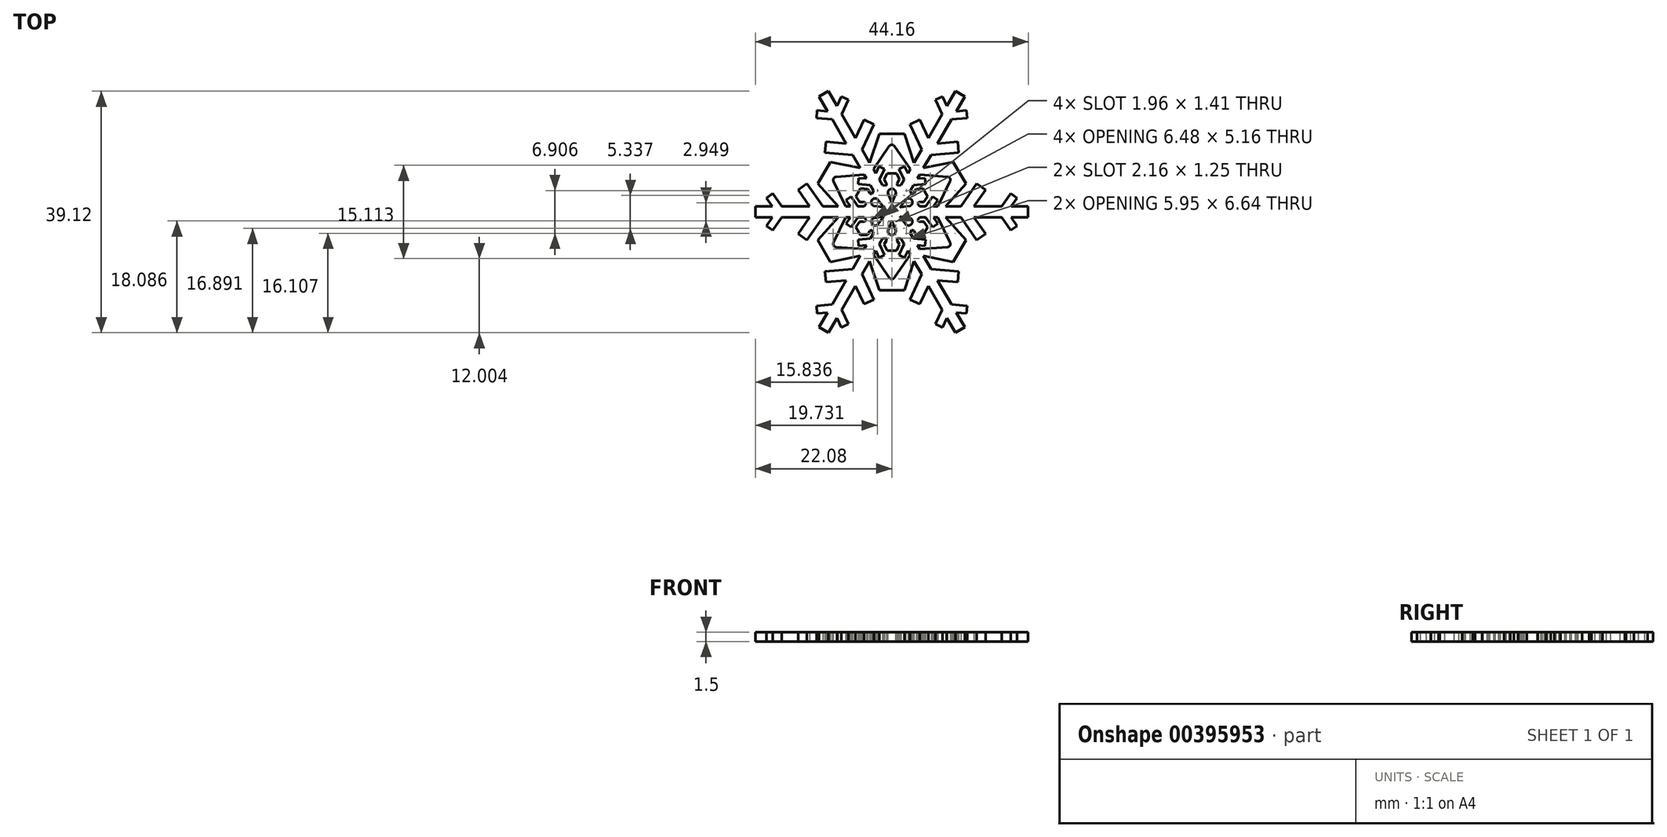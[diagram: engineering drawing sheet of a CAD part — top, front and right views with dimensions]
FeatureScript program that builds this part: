
annotation { "Feature Type Name" : "Feature", "Feature Type Description" : "" }
export const myFeature = defineFeature(function(context is Context, id is Id, definition is map)
    precondition{}
    {
        {
            var Q0;
            Q0=qCreatedBy(makeId("Top.planeOp"),FACE);
            var sketch = newSketch(context, id + "F0", { "sketchPlane" : qUnion([Q0])});
            skLineSegment(sketch, "E0.bottom", {"start": v(-43.7, 44.8) * mm, "end": v(41.1, 44.8) * mm});
            skLineSegment(sketch, "E0.top", {"start": v(-43.7, -40) * mm, "end": v(41.1, -40) * mm});
            skLineSegment(sketch, "E0.left", {"start": v(-43.7, 44.8) * mm, "end": v(-43.7, -40) * mm});
            skLineSegment(sketch, "E0.right", {"start": v(41.1, 44.8) * mm, "end": v(41.1, -40) * mm});
            skLineSegment(sketch, "E1", {"start": v(-44.15, 0) * mm, "end": v(-44.15, 1.75) * mm});
            skLineSegment(sketch, "E2", {"start": v(-44.15, 1.75) * mm, "end": v(-38.65, 1.75) * mm});
            skLineSegment(sketch, "E3", {"start": v(-38.65, 1.75) * mm, "end": v(-40.58, 4.5) * mm});
            skLineSegment(sketch, "E4", {"start": v(-40.58, 4.5) * mm, "end": v(-38.53, 5.94) * mm});
            skLineSegment(sketch, "E5", {"start": v(-38.53, 5.94) * mm, "end": v(-35.6, 1.75) * mm});
            skLineSegment(sketch, "E6", {"start": v(-35.6, 1.75) * mm, "end": v(-26.6, 1.75) * mm});
            skLineSegment(sketch, "E7", {"start": v(-26.6, 1.75) * mm, "end": v(-30.36, 7.13) * mm});
            skLineSegment(sketch, "E8", {"start": v(-30.36, 7.13) * mm, "end": v(-27.49, 9.13) * mm});
            skLineSegment(sketch, "E9", {"start": v(-27.49, 9.13) * mm, "end": v(-22.34, 1.75) * mm});
            skLineSegment(sketch, "E10", {"start": v(-22.34, 1.75) * mm, "end": v(-17.4, 1.75) * mm});
            skLineSegment(sketch, "E11", {"start": v(-14.94, 1.75) * mm, "end": v(-13.44, 1.75) * mm});
            skLineSegment(sketch, "E12", {"start": v(-13.44, 1.75) * mm, "end": v(-14.87, 3.8) * mm});
            skLineSegment(sketch, "E13", {"start": v(-14.87, 3.8) * mm, "end": v(-13.23, 4.94) * mm});
            skLineSegment(sketch, "E14", {"start": v(-13.23, 4.94) * mm, "end": v(-11, 1.75) * mm});
            skLineSegment(sketch, "E15", {"start": v(0, 0) * mm, "end": v(-44.15, 0) * mm, "construction": true});
            skLineSegment(sketch, "E16", {"start": v(-11, 1.75) * mm, "end": v(-8.98, 1.75) * mm});
            skLineSegment(sketch, "E17", {"start": v(0, 0) * mm, "end": v(-10.85, 6.27) * mm});
            skLineSegment(sketch, "E18", {"start": v(-8.98, 1.75) * mm, "end": v(-8.24, 2.67) * mm});
            skLineSegment(sketch, "E19", {"start": v(-8.24, 2.67) * mm, "end": v(-8.84, 3.15) * mm});
            skLineSegment(sketch, "E20", {"start": v(-8.84, 3.15) * mm, "end": v(-10.37, 3.15) * mm});
            skLineSegment(sketch, "E21", {"start": v(-10.37, 3.15) * mm, "end": v(-11.62, 4.94) * mm});
            skLineSegment(sketch, "E22", {"start": v(-11.62, 4.94) * mm, "end": v(-10.85, 6.27) * mm});
            skLineSegment(sketch, "E23", {"start": v(-10.85, 6.27) * mm, "end": v(-31.84, 18.38) * mm, "construction": true});
            skLineSegment(sketch, "E24", {"start": v(-23.98, 9.13) * mm, "end": v(-21.94, 12.67) * mm});
            skLineSegment(sketch, "E25", {"start": v(-14.94, 1.75) * mm, "end": v(-19.5, 11.26) * mm});
            skLineSegment(sketch, "E26", {"start": v(-23.98, 9.13) * mm, "end": v(-17.4, 1.75) * mm});
            skLineSegment(sketch, "E27", {"start": v(-21.94, 12.67) * mm, "end": v(-19.5, 11.26) * mm});
            skLineSegment(sketch, "E28.MirrorCS", {"start": v(0, 0) * mm, "end": v(-10.85, -6.27) * mm});
            skLineSegment(sketch, "E29.MirrorCS", {"start": v(-44.15, 0) * mm, "end": v(-44.15, -1.75) * mm});
            skLineSegment(sketch, "E30.MirrorCS", {"start": v(-14.94, -1.75) * mm, "end": v(-13.44, -1.75) * mm});
            skLineSegment(sketch, "E31.MirrorCS", {"start": v(-11.62, -4.94) * mm, "end": v(-10.85, -6.27) * mm});
            skLineSegment(sketch, "E32.MirrorCS", {"start": v(-14.87, -3.8) * mm, "end": v(-13.23, -4.94) * mm});
            skLineSegment(sketch, "E33.MirrorCS", {"start": v(-8.98, -1.75) * mm, "end": v(-8.24, -2.67) * mm});
            skLineSegment(sketch, "E34.MirrorCS", {"start": v(-8.84, -3.15) * mm, "end": v(-10.37, -3.15) * mm});
            skLineSegment(sketch, "E35.MirrorCS", {"start": v(-8.24, -2.67) * mm, "end": v(-8.84, -3.15) * mm});
            skLineSegment(sketch, "E36.MirrorCS", {"start": v(-14.94, -1.75) * mm, "end": v(-19.5, -11.26) * mm});
            skLineSegment(sketch, "E37.MirrorCS", {"start": v(-27.49, -9.13) * mm, "end": v(-22.34, -1.75) * mm});
            skLineSegment(sketch, "E38.MirrorCS", {"start": v(-21.94, -12.67) * mm, "end": v(-19.5, -11.26) * mm});
            skLineSegment(sketch, "E39.MirrorCS", {"start": v(-23.98, -9.13) * mm, "end": v(-21.94, -12.67) * mm});
            skLineSegment(sketch, "E40.MirrorCS", {"start": v(-11, -1.75) * mm, "end": v(-8.98, -1.75) * mm});
            skLineSegment(sketch, "E41.MirrorCS", {"start": v(-38.53, -5.94) * mm, "end": v(-35.6, -1.75) * mm});
            skLineSegment(sketch, "E42.MirrorCS", {"start": v(-40.58, -4.5) * mm, "end": v(-38.53, -5.94) * mm});
            skLineSegment(sketch, "E43.MirrorCS", {"start": v(-38.65, -1.75) * mm, "end": v(-40.58, -4.5) * mm});
            skLineSegment(sketch, "E44.MirrorCS", {"start": v(-44.15, -1.75) * mm, "end": v(-38.65, -1.75) * mm});
            skLineSegment(sketch, "E45.MirrorCS", {"start": v(-23.98, -9.13) * mm, "end": v(-17.4, -1.75) * mm});
            skLineSegment(sketch, "E46.MirrorCS", {"start": v(-30.36, -7.13) * mm, "end": v(-27.49, -9.13) * mm});
            skLineSegment(sketch, "E47.MirrorCS", {"start": v(-26.6, -1.75) * mm, "end": v(-30.36, -7.13) * mm});
            skLineSegment(sketch, "E48.MirrorCS", {"start": v(-35.6, -1.75) * mm, "end": v(-26.6, -1.75) * mm});
            skLineSegment(sketch, "E49.MirrorCS", {"start": v(-22.34, -1.75) * mm, "end": v(-17.4, -1.75) * mm});
            skLineSegment(sketch, "E50.MirrorCS", {"start": v(-13.44, -1.75) * mm, "end": v(-14.87, -3.8) * mm});
            skLineSegment(sketch, "E51.MirrorCS", {"start": v(-10.37, -3.15) * mm, "end": v(-11.62, -4.94) * mm});
            skLineSegment(sketch, "E52.MirrorCS", {"start": v(-13.23, -4.94) * mm, "end": v(-11, -1.75) * mm});
            skSolve(sketch);
        }
        {
            var Q0;
            Q0=makeQuery(id+"F0.imprint","IMPRINT",FACE,{"disambiguationData":[TD([[makeQuery(id+"F0.imprint","IMPRINT",EDGE,{"derivedFrom":sQuery(id+"F0.wireOp",EDGE,"E1")}),-1.0]])]});
            var Q1;
            {var subQ0=sQuery(id+"F0.wireOp",EDGE,"E3");Q1=makeQuery(id+"F0.imprint","IMPRINT",FACE,{"disambiguationData":[TD([[makeQuery(id+"F0.imprint","IMPRINT",EDGE,{"derivedFrom":subQ0}),-1.0]])]});}
            extrude(context, id + "F1", {"entities" : qUnion([Q0, Q1]), "endBound" : BoundingType.SYMMETRIC, "depth" : 3 * mm});
        }
        {
            var Q0;
            Q0=qCreatedBy(makeId("Right.planeOp"),FACE);
            var sketch = newSketch(context, id + "F2", { "sketchPlane" : qUnion([Q0])});
            skLineSegment(sketch, "E53", {"start": v(0, 0) * mm, "end": v(0, -43.45) * mm, "construction": true});
            skSolve(sketch);
        }
        {
            var Q0;
            Q0=makeQuery(id+"F1.opExtrude","SWEPT_BODY",BODY,{"disambiguationData":[OSD([sQuery(id+"F0.wireOp",EDGE,"E1"),sQuery(id+"F0.wireOp",EDGE,"E2"),sQuery(id+"F0.wireOp",EDGE,"E3"),sQuery(id+"F0.wireOp",EDGE,"E4"),sQuery(id+"F0.wireOp",EDGE,"E5"),sQuery(id+"F0.wireOp",EDGE,"E6"),sQuery(id+"F0.wireOp",EDGE,"E7"),sQuery(id+"F0.wireOp",EDGE,"E8"),sQuery(id+"F0.wireOp",EDGE,"E9"),sQuery(id+"F0.wireOp",EDGE,"E10"),sQuery(id+"F0.wireOp",EDGE,"189a7a4e-f39c-4bfd-b122-43a29ca94680"),sQuery(id+"F0.wireOp",EDGE,"67050dc1-3990-4a49-9707-dffdccfb30a0"),sQuery(id+"F0.wireOp",EDGE,"437a0215-fb6c-4063-ad75-b84b83856d58"),sQuery(id+"F0.wireOp",EDGE,"E11"),sQuery(id+"F0.wireOp",EDGE,"E12"),sQuery(id+"F0.wireOp",EDGE,"E13"),sQuery(id+"F0.wireOp",EDGE,"E14"),sQuery(id+"F0.wireOp",EDGE,"5e9898c1-a996-4e9f-834a-20b7154747a1"),sQuery(id+"F0.wireOp",EDGE,"4f175b08-8b9f-4015-be58-81c3dce13333"),sQuery(id+"F0.wireOp",EDGE,"3166d6ec-2b74-46b0-8a25-8ff819b97b050.MirrorCS"),sQuery(id+"F0.wireOp",EDGE,"3166d6ec-2b74-46b0-8a25-8ff819b97b051.MirrorCS"),sQuery(id+"F0.wireOp",EDGE,"3166d6ec-2b74-46b0-8a25-8ff819b97b052.MirrorCS"),sQuery(id+"F0.wireOp",EDGE,"3166d6ec-2b74-46b0-8a25-8ff819b97b053.MirrorCS"),sQuery(id+"F0.wireOp",EDGE,"3166d6ec-2b74-46b0-8a25-8ff819b97b054.MirrorCS"),sQuery(id+"F0.wireOp",EDGE,"3166d6ec-2b74-46b0-8a25-8ff819b97b055.MirrorCS"),sQuery(id+"F0.wireOp",EDGE,"3166d6ec-2b74-46b0-8a25-8ff819b97b056.MirrorCS"),sQuery(id+"F0.wireOp",EDGE,"3166d6ec-2b74-46b0-8a25-8ff819b97b057.MirrorCS"),sQuery(id+"F0.wireOp",EDGE,"3166d6ec-2b74-46b0-8a25-8ff819b97b058.MirrorCS"),sQuery(id+"F0.wireOp",EDGE,"3166d6ec-2b74-46b0-8a25-8ff819b97b059.MirrorCS"),sQuery(id+"F0.wireOp",EDGE,"3166d6ec-2b74-46b0-8a25-8ff819b97b0510.MirrorCS"),sQuery(id+"F0.wireOp",EDGE,"3166d6ec-2b74-46b0-8a25-8ff819b97b0511.MirrorCS"),sQuery(id+"F0.wireOp",EDGE,"3166d6ec-2b74-46b0-8a25-8ff819b97b0512.MirrorCS"),sQuery(id+"F0.wireOp",EDGE,"3166d6ec-2b74-46b0-8a25-8ff819b97b0513.MirrorCS"),sQuery(id+"F0.wireOp",EDGE,"3166d6ec-2b74-46b0-8a25-8ff819b97b0514.MirrorCS"),sQuery(id+"F0.wireOp",EDGE,"3166d6ec-2b74-46b0-8a25-8ff819b97b0515.MirrorCS"),sQuery(id+"F0.wireOp",EDGE,"3166d6ec-2b74-46b0-8a25-8ff819b97b0516.MirrorCS"),sQuery(id+"F0.wireOp",EDGE,"3166d6ec-2b74-46b0-8a25-8ff819b97b0517.MirrorCS"),sQuery(id+"F0.wireOp",EDGE,"3166d6ec-2b74-46b0-8a25-8ff819b97b0518.MirrorCS")])]});
            var Q1;
            Q1=sQuery(id+"F2.wireOp",EDGE,"E53");
            circularPattern(context, id + "F3", {"operationType" : NewBodyOperationType.ADD, "entities" : qUnion([Q0]), "axis" : qUnion([Q1]), "angle" : 60 * degree, "instanceCount" : 6});
        }
        {
            var Q0;
            {var subQ0=makeQuery(id+"F1.opExtrude","CAP_FACE",FACE,{"disambiguationData":[OSD([sQuery(id+"F0.wireOp",EDGE,"E1"),sQuery(id+"F0.wireOp",EDGE,"E2"),sQuery(id+"F0.wireOp",EDGE,"E3"),sQuery(id+"F0.wireOp",EDGE,"E4"),sQuery(id+"F0.wireOp",EDGE,"E5"),sQuery(id+"F0.wireOp",EDGE,"E6"),sQuery(id+"F0.wireOp",EDGE,"E7"),sQuery(id+"F0.wireOp",EDGE,"E8"),sQuery(id+"F0.wireOp",EDGE,"E9"),sQuery(id+"F0.wireOp",EDGE,"E10"),sQuery(id+"F0.wireOp",EDGE,"189a7a4e-f39c-4bfd-b122-43a29ca94680"),sQuery(id+"F0.wireOp",EDGE,"67050dc1-3990-4a49-9707-dffdccfb30a0"),sQuery(id+"F0.wireOp",EDGE,"437a0215-fb6c-4063-ad75-b84b83856d58"),sQuery(id+"F0.wireOp",EDGE,"E11"),sQuery(id+"F0.wireOp",EDGE,"E12"),sQuery(id+"F0.wireOp",EDGE,"E13"),sQuery(id+"F0.wireOp",EDGE,"E14"),sQuery(id+"F0.wireOp",EDGE,"E16"),sQuery(id+"F0.wireOp",EDGE,"E17"),sQuery(id+"F0.wireOp",EDGE,"E18"),sQuery(id+"F0.wireOp",EDGE,"E19"),sQuery(id+"F0.wireOp",EDGE,"E20"),sQuery(id+"F0.wireOp",EDGE,"E21"),sQuery(id+"F0.wireOp",EDGE,"E22"),sQuery(id+"F0.wireOp",EDGE,"0c32c283-354d-45ec-8926-575daeb4bd260.MirrorCS"),sQuery(id+"F0.wireOp",EDGE,"0c32c283-354d-45ec-8926-575daeb4bd261.MirrorCS"),sQuery(id+"F0.wireOp",EDGE,"0c32c283-354d-45ec-8926-575daeb4bd262.MirrorCS"),sQuery(id+"F0.wireOp",EDGE,"0c32c283-354d-45ec-8926-575daeb4bd263.MirrorCS"),sQuery(id+"F0.wireOp",EDGE,"0c32c283-354d-45ec-8926-575daeb4bd264.MirrorCS"),sQuery(id+"F0.wireOp",EDGE,"0c32c283-354d-45ec-8926-575daeb4bd265.MirrorCS"),sQuery(id+"F0.wireOp",EDGE,"0c32c283-354d-45ec-8926-575daeb4bd266.MirrorCS"),sQuery(id+"F0.wireOp",EDGE,"0c32c283-354d-45ec-8926-575daeb4bd267.MirrorCS"),sQuery(id+"F0.wireOp",EDGE,"0c32c283-354d-45ec-8926-575daeb4bd268.MirrorCS"),sQuery(id+"F0.wireOp",EDGE,"0c32c283-354d-45ec-8926-575daeb4bd269.MirrorCS"),sQuery(id+"F0.wireOp",EDGE,"0c32c283-354d-45ec-8926-575daeb4bd2610.MirrorCS"),sQuery(id+"F0.wireOp",EDGE,"0c32c283-354d-45ec-8926-575daeb4bd2611.MirrorCS"),sQuery(id+"F0.wireOp",EDGE,"0c32c283-354d-45ec-8926-575daeb4bd2612.MirrorCS"),sQuery(id+"F0.wireOp",EDGE,"0c32c283-354d-45ec-8926-575daeb4bd2613.MirrorCS"),sQuery(id+"F0.wireOp",EDGE,"0c32c283-354d-45ec-8926-575daeb4bd2614.MirrorCS"),sQuery(id+"F0.wireOp",EDGE,"0c32c283-354d-45ec-8926-575daeb4bd2615.MirrorCS"),sQuery(id+"F0.wireOp",EDGE,"0c32c283-354d-45ec-8926-575daeb4bd2616.MirrorCS"),sQuery(id+"F0.wireOp",EDGE,"0c32c283-354d-45ec-8926-575daeb4bd2617.MirrorCS"),sQuery(id+"F0.wireOp",EDGE,"0c32c283-354d-45ec-8926-575daeb4bd2618.MirrorCS"),sQuery(id+"F0.wireOp",EDGE,"0c32c283-354d-45ec-8926-575daeb4bd2619.MirrorCS"),sQuery(id+"F0.wireOp",EDGE,"0c32c283-354d-45ec-8926-575daeb4bd2620.MirrorCS"),sQuery(id+"F0.wireOp",EDGE,"0c32c283-354d-45ec-8926-575daeb4bd2621.MirrorCS"),sQuery(id+"F0.wireOp",EDGE,"0c32c283-354d-45ec-8926-575daeb4bd2622.MirrorCS"),sQuery(id+"F0.wireOp",EDGE,"0c32c283-354d-45ec-8926-575daeb4bd2623.MirrorCS")])],"isStart":false});Q0=makeQuery(id+"F3.boolean.opBoolean","MERGE",FACE,{"derivedFrom":[subQ0,makeQuery(id+"F3.opPattern","COPY",FACE,{"derivedFrom":subQ0,"instanceName":"1"}),makeQuery(id+"F3.opPattern","COPY",FACE,{"derivedFrom":subQ0,"instanceName":"2"}),makeQuery(id+"F3.opPattern","COPY",FACE,{"derivedFrom":subQ0,"instanceName":"3"}),makeQuery(id+"F3.opPattern","COPY",FACE,{"derivedFrom":subQ0,"instanceName":"4"}),makeQuery(id+"F3.opPattern","COPY",FACE,{"derivedFrom":subQ0,"instanceName":"5"})]});}
            var sketch = newSketch(context, id + "F4", { "sketchPlane" : qUnion([Q0])});
            skLineSegment(sketch, "E54", {"start": v(0, 0) * mm, "end": v(-10.85, 6.27) * mm, "construction": true});
            skLineSegment(sketch, "E55", {"start": v(-6.5, 3.75) * mm, "end": v(-2.6, 1.5) * mm, "construction": true});
            skLineSegment(sketch, "E56", {"start": v(-5.87, 1.94) * mm, "end": v(-2.6, 1.5) * mm});
            skLineSegment(sketch, "E57.MirrorCS", {"start": v(-4.62, 4.1) * mm, "end": v(-2.6, 1.5) * mm});
            skLineSegment(sketch, "E58", {"start": v(-5.87, 1.94) * mm, "end": v(-4.62, 4.1) * mm, "construction": true});
            skArc(sketch, "E59", {"start": v(-4.62, 4.1) * mm, "mid": v(-6.5, 3.75) * mm, "end": v(-5.87, 1.94) * mm});
            skSolve(sketch);
        }
        {
            var Q0;
            Q0=makeQuery(id+"F4.imprint","IMPRINT",FACE,{"disambiguationData":[TD([[makeQuery(id+"F4.imprint","IMPRINT",EDGE,{"derivedFrom":sQuery(id+"F4.wireOp",EDGE,"980073ca-cf30-472a-b92e-9ee7ff5da41c")}),1.0]])]});
            var Q1;
            Q1=makeQuery(id+"F4.imprint","IMPRINT",FACE,{"disambiguationData":[TD([[makeQuery(id+"F4.imprint","IMPRINT",EDGE,{"derivedFrom":sQuery(id+"F4.wireOp",EDGE,"E56")}),1.0]])]});
            extrude(context, id + "F5", {"entities" : qUnion([Q0, Q1]), "operationType" : NewBodyOperationType.REMOVE, "endBound" : BoundingType.UP_TO_NEXT, "oppositeDirection" : true, "depth" : 25 * mm});
        }
        {
            var Q0;
            Q0=makeQuery(id+"F5.boolean.opBoolean","COPY",EDGE,{"derivedFrom":makeQuery(id+"F5.opExtrude","SWEPT_EDGE",EDGE,{"disambiguationData":[OSD([sQuery(id+"F4.wireOp",EDGE,"E56"),sQuery(id+"F4.wireOp",EDGE,"E57.MirrorCS")])]})});
            fillet(context, id + "F6", {"entities" : qUnion([Q0]), "radius" : 0.1 * mm, "tangentPropagation" : true, "allowEdgeOverflow" : false});
        }
        {
            var Q0;
            Q0=makeQuery(id+"F5.boolean.opBoolean","COPY",FACE,{"derivedFrom":makeQuery(id+"F5.opExtrude","SWEPT_FACE",FACE,{"disambiguationData":[OSD([sQuery(id+"F4.wireOp",EDGE,"E59")])]})});
            var Q1;
            Q1=makeQuery(id+"F5.boolean.opBoolean","COPY",FACE,{"derivedFrom":makeQuery(id+"F5.opExtrude","SWEPT_FACE",FACE,{"disambiguationData":[OSD([sQuery(id+"F4.wireOp",EDGE,"E56")])]})});
            var Q2;
            Q2=makeQuery(id+"F5.boolean.opBoolean","COPY",FACE,{"derivedFrom":makeQuery(id+"F5.opExtrude","SWEPT_FACE",FACE,{"disambiguationData":[OSD([sQuery(id+"F4.wireOp",EDGE,"E57.MirrorCS")])]})});
            var Q3;
            Q3=makeQuery(id+"F6.opFillet","BLEND_FACE",FACE,{"disambiguationData":[OSD([sQuery(id+"F4.wireOp",EDGE,"E56"),sQuery(id+"F4.wireOp",EDGE,"E57.MirrorCS")])]});
            var Q4;
            Q4=sQuery(id+"F2.wireOp",EDGE,"E53");
            circularPattern(context, id + "F7", {"faces" : qUnion([Q0, Q1, Q2, Q3]), "axis" : qUnion([Q4]), "angle" : 60 * degree, "instanceCount" : 6, "patternType" : PatternType.FACE});
        }
        {
            var Q0;
            {var subQ0=makeQuery(id+"F1.opExtrude","CAP_FACE",FACE,{"disambiguationData":[OSD([sQuery(id+"F0.wireOp",EDGE,"E1"),sQuery(id+"F0.wireOp",EDGE,"E2"),sQuery(id+"F0.wireOp",EDGE,"E3"),sQuery(id+"F0.wireOp",EDGE,"E4"),sQuery(id+"F0.wireOp",EDGE,"E5"),sQuery(id+"F0.wireOp",EDGE,"E6"),sQuery(id+"F0.wireOp",EDGE,"E7"),sQuery(id+"F0.wireOp",EDGE,"E8"),sQuery(id+"F0.wireOp",EDGE,"E9"),sQuery(id+"F0.wireOp",EDGE,"E10"),sQuery(id+"F0.wireOp",EDGE,"189a7a4e-f39c-4bfd-b122-43a29ca94680"),sQuery(id+"F0.wireOp",EDGE,"67050dc1-3990-4a49-9707-dffdccfb30a0"),sQuery(id+"F0.wireOp",EDGE,"437a0215-fb6c-4063-ad75-b84b83856d58"),sQuery(id+"F0.wireOp",EDGE,"E11"),sQuery(id+"F0.wireOp",EDGE,"E12"),sQuery(id+"F0.wireOp",EDGE,"E13"),sQuery(id+"F0.wireOp",EDGE,"E14"),sQuery(id+"F0.wireOp",EDGE,"E16"),sQuery(id+"F0.wireOp",EDGE,"E17"),sQuery(id+"F0.wireOp",EDGE,"E18"),sQuery(id+"F0.wireOp",EDGE,"E19"),sQuery(id+"F0.wireOp",EDGE,"E20"),sQuery(id+"F0.wireOp",EDGE,"E21"),sQuery(id+"F0.wireOp",EDGE,"E22"),sQuery(id+"F0.wireOp",EDGE,"0c32c283-354d-45ec-8926-575daeb4bd260.MirrorCS"),sQuery(id+"F0.wireOp",EDGE,"0c32c283-354d-45ec-8926-575daeb4bd261.MirrorCS"),sQuery(id+"F0.wireOp",EDGE,"0c32c283-354d-45ec-8926-575daeb4bd262.MirrorCS"),sQuery(id+"F0.wireOp",EDGE,"0c32c283-354d-45ec-8926-575daeb4bd263.MirrorCS"),sQuery(id+"F0.wireOp",EDGE,"0c32c283-354d-45ec-8926-575daeb4bd264.MirrorCS"),sQuery(id+"F0.wireOp",EDGE,"0c32c283-354d-45ec-8926-575daeb4bd265.MirrorCS"),sQuery(id+"F0.wireOp",EDGE,"0c32c283-354d-45ec-8926-575daeb4bd266.MirrorCS"),sQuery(id+"F0.wireOp",EDGE,"0c32c283-354d-45ec-8926-575daeb4bd267.MirrorCS"),sQuery(id+"F0.wireOp",EDGE,"0c32c283-354d-45ec-8926-575daeb4bd268.MirrorCS"),sQuery(id+"F0.wireOp",EDGE,"0c32c283-354d-45ec-8926-575daeb4bd269.MirrorCS"),sQuery(id+"F0.wireOp",EDGE,"0c32c283-354d-45ec-8926-575daeb4bd2610.MirrorCS"),sQuery(id+"F0.wireOp",EDGE,"0c32c283-354d-45ec-8926-575daeb4bd2611.MirrorCS"),sQuery(id+"F0.wireOp",EDGE,"0c32c283-354d-45ec-8926-575daeb4bd2612.MirrorCS"),sQuery(id+"F0.wireOp",EDGE,"0c32c283-354d-45ec-8926-575daeb4bd2613.MirrorCS"),sQuery(id+"F0.wireOp",EDGE,"0c32c283-354d-45ec-8926-575daeb4bd2614.MirrorCS"),sQuery(id+"F0.wireOp",EDGE,"0c32c283-354d-45ec-8926-575daeb4bd2615.MirrorCS"),sQuery(id+"F0.wireOp",EDGE,"0c32c283-354d-45ec-8926-575daeb4bd2616.MirrorCS"),sQuery(id+"F0.wireOp",EDGE,"0c32c283-354d-45ec-8926-575daeb4bd2617.MirrorCS"),sQuery(id+"F0.wireOp",EDGE,"0c32c283-354d-45ec-8926-575daeb4bd2618.MirrorCS"),sQuery(id+"F0.wireOp",EDGE,"0c32c283-354d-45ec-8926-575daeb4bd2619.MirrorCS"),sQuery(id+"F0.wireOp",EDGE,"0c32c283-354d-45ec-8926-575daeb4bd2620.MirrorCS"),sQuery(id+"F0.wireOp",EDGE,"0c32c283-354d-45ec-8926-575daeb4bd2621.MirrorCS"),sQuery(id+"F0.wireOp",EDGE,"0c32c283-354d-45ec-8926-575daeb4bd2622.MirrorCS"),sQuery(id+"F0.wireOp",EDGE,"0c32c283-354d-45ec-8926-575daeb4bd2623.MirrorCS")])],"isStart":false});Q0=makeQuery(id+"F3.boolean.opBoolean","MERGE",FACE,{"derivedFrom":[subQ0,makeQuery(id+"F3.opPattern","COPY",FACE,{"derivedFrom":subQ0,"instanceName":"1"}),makeQuery(id+"F3.opPattern","COPY",FACE,{"derivedFrom":subQ0,"instanceName":"2"}),makeQuery(id+"F3.opPattern","COPY",FACE,{"derivedFrom":subQ0,"instanceName":"3"}),makeQuery(id+"F3.opPattern","COPY",FACE,{"derivedFrom":subQ0,"instanceName":"4"}),makeQuery(id+"F3.opPattern","COPY",FACE,{"derivedFrom":subQ0,"instanceName":"5"})]});}
            var sketch = newSketch(context, id + "F8", { "sketchPlane" : qUnion([Q0])});
            skArc(sketch, "E60", {"start": v(-44.15, 1.75) * mm, "mid": v(-51.75, 0) * mm, "end": v(-44.15, -1.75) * mm});
            skCircle(sketch, "E61", {"center": v(-47.75, 0) * mm, "radius": 2 * mm});
            skSolve(sketch);
        }
        {
            var Q0;
            Q0=makeQuery(id+"F8.imprint","IMPRINT",FACE,{"disambiguationData":[TD([[makeQuery(id+"F8.imprint","IMPRINT",EDGE,{"derivedFrom":sQuery(id+"F8.wireOp",EDGE,"E60")}),1.0]])]});
            extrude(context, id + "F9", {"entities" : qUnion([Q0]), "operationType" : NewBodyOperationType.ADD, "oppositeDirection" : true, "depth" : 3 * mm});
        }
        {
            var Q0;
            Q0=makeQuery(id+"F3.boolean.opBoolean","MERGE",EDGE,{"derivedFrom":[makeQuery(id+"F1.opExtrude","SWEPT_EDGE",EDGE,{"disambiguationData":[OSD([sQuery(id+"F0.wireOp",EDGE,"E25"),sQuery(id+"F0.wireOp",EDGE,"E27")])]}),makeQuery(id+"F3.opPattern","COPY",EDGE,{"derivedFrom":makeQuery(id+"F1.opExtrude","SWEPT_EDGE",EDGE,{"disambiguationData":[OSD([sQuery(id+"F0.wireOp",EDGE,"E36.MirrorCS"),sQuery(id+"F0.wireOp",EDGE,"E38.MirrorCS")])]}),"instanceName":"1"})]});
            var Q1;
            Q1=makeQuery(id+"F3.boolean.opBoolean","MERGE",EDGE,{"derivedFrom":[makeQuery(id+"F1.opExtrude","SWEPT_EDGE",EDGE,{"disambiguationData":[OSD([sQuery(id+"F0.wireOp",EDGE,"E36.MirrorCS"),sQuery(id+"F0.wireOp",EDGE,"E38.MirrorCS")])]}),makeQuery(id+"F3.opPattern","COPY",EDGE,{"derivedFrom":makeQuery(id+"F1.opExtrude","SWEPT_EDGE",EDGE,{"disambiguationData":[OSD([sQuery(id+"F0.wireOp",EDGE,"E25"),sQuery(id+"F0.wireOp",EDGE,"E27")])]}),"instanceName":"5"})]});
            var Q2;
            Q2=makeQuery(id+"F3.boolean.opBoolean","MERGE",EDGE,{"derivedFrom":[makeQuery(id+"F3.opPattern","COPY",EDGE,{"derivedFrom":makeQuery(id+"F1.opExtrude","SWEPT_EDGE",EDGE,{"disambiguationData":[OSD([sQuery(id+"F0.wireOp",EDGE,"E25"),sQuery(id+"F0.wireOp",EDGE,"E27")])]}),"instanceName":"4"}),makeQuery(id+"F3.opPattern","COPY",EDGE,{"derivedFrom":makeQuery(id+"F1.opExtrude","SWEPT_EDGE",EDGE,{"disambiguationData":[OSD([sQuery(id+"F0.wireOp",EDGE,"E36.MirrorCS"),sQuery(id+"F0.wireOp",EDGE,"E38.MirrorCS")])]}),"instanceName":"5"})]});
            var Q3;
            Q3=makeQuery(id+"F3.boolean.opBoolean","MERGE",EDGE,{"derivedFrom":[makeQuery(id+"F3.opPattern","COPY",EDGE,{"derivedFrom":makeQuery(id+"F1.opExtrude","SWEPT_EDGE",EDGE,{"disambiguationData":[OSD([sQuery(id+"F0.wireOp",EDGE,"E25"),sQuery(id+"F0.wireOp",EDGE,"E27")])]}),"instanceName":"3"}),makeQuery(id+"F3.opPattern","COPY",EDGE,{"derivedFrom":makeQuery(id+"F1.opExtrude","SWEPT_EDGE",EDGE,{"disambiguationData":[OSD([sQuery(id+"F0.wireOp",EDGE,"E36.MirrorCS"),sQuery(id+"F0.wireOp",EDGE,"E38.MirrorCS")])]}),"instanceName":"4"})]});
            var Q4;
            Q4=makeQuery(id+"F3.boolean.opBoolean","MERGE",EDGE,{"derivedFrom":[makeQuery(id+"F3.opPattern","COPY",EDGE,{"derivedFrom":makeQuery(id+"F1.opExtrude","SWEPT_EDGE",EDGE,{"disambiguationData":[OSD([sQuery(id+"F0.wireOp",EDGE,"E25"),sQuery(id+"F0.wireOp",EDGE,"E27")])]}),"instanceName":"1"}),makeQuery(id+"F3.opPattern","COPY",EDGE,{"derivedFrom":makeQuery(id+"F1.opExtrude","SWEPT_EDGE",EDGE,{"disambiguationData":[OSD([sQuery(id+"F0.wireOp",EDGE,"E36.MirrorCS"),sQuery(id+"F0.wireOp",EDGE,"E38.MirrorCS")])]}),"instanceName":"2"})]});
            var Q5;
            Q5=makeQuery(id+"F3.boolean.opBoolean","MERGE",EDGE,{"derivedFrom":[makeQuery(id+"F3.opPattern","COPY",EDGE,{"derivedFrom":makeQuery(id+"F1.opExtrude","SWEPT_EDGE",EDGE,{"disambiguationData":[OSD([sQuery(id+"F0.wireOp",EDGE,"E25"),sQuery(id+"F0.wireOp",EDGE,"E27")])]}),"instanceName":"2"}),makeQuery(id+"F3.opPattern","COPY",EDGE,{"derivedFrom":makeQuery(id+"F1.opExtrude","SWEPT_EDGE",EDGE,{"disambiguationData":[OSD([sQuery(id+"F0.wireOp",EDGE,"E36.MirrorCS"),sQuery(id+"F0.wireOp",EDGE,"E38.MirrorCS")])]}),"instanceName":"3"})]});
            fillet(context, id + "F10", {"entities" : qUnion([Q0, Q1, Q2, Q3, Q4, Q5]), "radius" : 1 * mm, "tangentPropagation" : true, "allowEdgeOverflow" : false});
        }
        {
            var Q0;
            {var subQ0=sQuery(id+"F0.wireOp",EDGE,"E29.MirrorCS");var subQ1=sQuery(id+"F0.wireOp",EDGE,"E1");var subQ2=makeQuery(id+"F1.opExtrude","CAP_FACE",FACE,{"disambiguationData":[OSD([subQ1,sQuery(id+"F0.wireOp",EDGE,"E2"),sQuery(id+"F0.wireOp",EDGE,"E3"),sQuery(id+"F0.wireOp",EDGE,"E4"),sQuery(id+"F0.wireOp",EDGE,"E5"),sQuery(id+"F0.wireOp",EDGE,"E6"),sQuery(id+"F0.wireOp",EDGE,"E7"),sQuery(id+"F0.wireOp",EDGE,"E8"),sQuery(id+"F0.wireOp",EDGE,"E9"),sQuery(id+"F0.wireOp",EDGE,"E10"),sQuery(id+"F0.wireOp",EDGE,"E11"),sQuery(id+"F0.wireOp",EDGE,"E12"),sQuery(id+"F0.wireOp",EDGE,"E13"),sQuery(id+"F0.wireOp",EDGE,"E14"),sQuery(id+"F0.wireOp",EDGE,"E16"),sQuery(id+"F0.wireOp",EDGE,"E17"),sQuery(id+"F0.wireOp",EDGE,"E18"),sQuery(id+"F0.wireOp",EDGE,"E19"),sQuery(id+"F0.wireOp",EDGE,"E20"),sQuery(id+"F0.wireOp",EDGE,"E21"),sQuery(id+"F0.wireOp",EDGE,"E22"),sQuery(id+"F0.wireOp",EDGE,"E24"),sQuery(id+"F0.wireOp",EDGE,"E25"),sQuery(id+"F0.wireOp",EDGE,"E26"),sQuery(id+"F0.wireOp",EDGE,"E27"),sQuery(id+"F0.wireOp",EDGE,"E28.MirrorCS"),subQ0,sQuery(id+"F0.wireOp",EDGE,"E30.MirrorCS"),sQuery(id+"F0.wireOp",EDGE,"E31.MirrorCS"),sQuery(id+"F0.wireOp",EDGE,"E32.MirrorCS"),sQuery(id+"F0.wireOp",EDGE,"E33.MirrorCS"),sQuery(id+"F0.wireOp",EDGE,"E34.MirrorCS"),sQuery(id+"F0.wireOp",EDGE,"E35.MirrorCS"),sQuery(id+"F0.wireOp",EDGE,"E36.MirrorCS"),sQuery(id+"F0.wireOp",EDGE,"E37.MirrorCS"),sQuery(id+"F0.wireOp",EDGE,"E38.MirrorCS"),sQuery(id+"F0.wireOp",EDGE,"E39.MirrorCS"),sQuery(id+"F0.wireOp",EDGE,"E40.MirrorCS"),sQuery(id+"F0.wireOp",EDGE,"E41.MirrorCS"),sQuery(id+"F0.wireOp",EDGE,"E42.MirrorCS"),sQuery(id+"F0.wireOp",EDGE,"E43.MirrorCS"),sQuery(id+"F0.wireOp",EDGE,"E44.MirrorCS"),sQuery(id+"F0.wireOp",EDGE,"E45.MirrorCS"),sQuery(id+"F0.wireOp",EDGE,"E46.MirrorCS"),sQuery(id+"F0.wireOp",EDGE,"E47.MirrorCS"),sQuery(id+"F0.wireOp",EDGE,"E48.MirrorCS"),sQuery(id+"F0.wireOp",EDGE,"E49.MirrorCS"),sQuery(id+"F0.wireOp",EDGE,"E50.MirrorCS"),sQuery(id+"F0.wireOp",EDGE,"E51.MirrorCS"),sQuery(id+"F0.wireOp",EDGE,"E52.MirrorCS")])],"isStart":false});Q0=makeQuery(id+"F9.boolean.opBoolean","MERGE",FACE,{"derivedFrom":[makeQuery(id+"F3.boolean.opBoolean","MERGE",FACE,{"derivedFrom":[subQ2,makeQuery(id+"F3.opPattern","COPY",FACE,{"derivedFrom":subQ2,"instanceName":"1"}),makeQuery(id+"F3.opPattern","COPY",FACE,{"derivedFrom":subQ2,"instanceName":"2"}),makeQuery(id+"F3.opPattern","COPY",FACE,{"derivedFrom":subQ2,"instanceName":"3"}),makeQuery(id+"F3.opPattern","COPY",FACE,{"derivedFrom":subQ2,"instanceName":"4"}),makeQuery(id+"F3.opPattern","COPY",FACE,{"derivedFrom":subQ2,"instanceName":"5"})]}),makeQuery(id+"F9.opExtrude","CAP_FACE",FACE,{"disambiguationData":[OSD([subQ1,subQ0,sQuery(id+"F8.wireOp",EDGE,"E60"),sQuery(id+"F8.wireOp",EDGE,"E61")])],"isStart":true})]});}
            var sketch = newSketch(context, id + "F11", { "sketchPlane" : qUnion([Q0])});
            skLineSegment(sketch, "E62", {"start": v(-44.15, -1.75) * mm, "end": v(-44.15, 1.75) * mm});
            skSolve(sketch);
        }
        {
            var Q0;
            Q0=makeQuery(id+"F11.imprint","IMPRINT",FACE,{"disambiguationData":[TD([[makeQuery(id+"F11.imprint","IMPRINT",EDGE,{"derivedFrom":sQuery(id+"F11.wireOp",EDGE,"E62")}),1.0]])]});
            extrude(context, id + "F12", {"entities" : qUnion([Q0]), "operationType" : NewBodyOperationType.REMOVE, "oppositeDirection" : true, "depth" : 25 * mm});
        }
        {
            var Q0;
            Q0=makeQuery(id+"F1.opExtrude","SWEPT_BODY",BODY,{"disambiguationData":[OSD([sQuery(id+"F0.wireOp",EDGE,"E1"),sQuery(id+"F0.wireOp",EDGE,"E2"),sQuery(id+"F0.wireOp",EDGE,"E3"),sQuery(id+"F0.wireOp",EDGE,"E4"),sQuery(id+"F0.wireOp",EDGE,"E5"),sQuery(id+"F0.wireOp",EDGE,"E6"),sQuery(id+"F0.wireOp",EDGE,"E7"),sQuery(id+"F0.wireOp",EDGE,"E8"),sQuery(id+"F0.wireOp",EDGE,"E9"),sQuery(id+"F0.wireOp",EDGE,"E10"),sQuery(id+"F0.wireOp",EDGE,"E11"),sQuery(id+"F0.wireOp",EDGE,"E12"),sQuery(id+"F0.wireOp",EDGE,"E13"),sQuery(id+"F0.wireOp",EDGE,"E14"),sQuery(id+"F0.wireOp",EDGE,"E16"),sQuery(id+"F0.wireOp",EDGE,"E17"),sQuery(id+"F0.wireOp",EDGE,"E18"),sQuery(id+"F0.wireOp",EDGE,"E19"),sQuery(id+"F0.wireOp",EDGE,"E20"),sQuery(id+"F0.wireOp",EDGE,"E21"),sQuery(id+"F0.wireOp",EDGE,"E22"),sQuery(id+"F0.wireOp",EDGE,"E24"),sQuery(id+"F0.wireOp",EDGE,"E25"),sQuery(id+"F0.wireOp",EDGE,"E26"),sQuery(id+"F0.wireOp",EDGE,"E27"),sQuery(id+"F0.wireOp",EDGE,"E28.MirrorCS"),sQuery(id+"F0.wireOp",EDGE,"E29.MirrorCS"),sQuery(id+"F0.wireOp",EDGE,"E30.MirrorCS"),sQuery(id+"F0.wireOp",EDGE,"E31.MirrorCS"),sQuery(id+"F0.wireOp",EDGE,"E32.MirrorCS"),sQuery(id+"F0.wireOp",EDGE,"E33.MirrorCS"),sQuery(id+"F0.wireOp",EDGE,"E34.MirrorCS"),sQuery(id+"F0.wireOp",EDGE,"E35.MirrorCS"),sQuery(id+"F0.wireOp",EDGE,"E36.MirrorCS"),sQuery(id+"F0.wireOp",EDGE,"E37.MirrorCS"),sQuery(id+"F0.wireOp",EDGE,"E38.MirrorCS"),sQuery(id+"F0.wireOp",EDGE,"E39.MirrorCS"),sQuery(id+"F0.wireOp",EDGE,"E40.MirrorCS"),sQuery(id+"F0.wireOp",EDGE,"E41.MirrorCS"),sQuery(id+"F0.wireOp",EDGE,"E42.MirrorCS"),sQuery(id+"F0.wireOp",EDGE,"E43.MirrorCS"),sQuery(id+"F0.wireOp",EDGE,"E44.MirrorCS"),sQuery(id+"F0.wireOp",EDGE,"E45.MirrorCS"),sQuery(id+"F0.wireOp",EDGE,"E46.MirrorCS"),sQuery(id+"F0.wireOp",EDGE,"E47.MirrorCS"),sQuery(id+"F0.wireOp",EDGE,"E48.MirrorCS"),sQuery(id+"F0.wireOp",EDGE,"E49.MirrorCS"),sQuery(id+"F0.wireOp",EDGE,"E50.MirrorCS"),sQuery(id+"F0.wireOp",EDGE,"E51.MirrorCS"),sQuery(id+"F0.wireOp",EDGE,"E52.MirrorCS")])]});
            var Q1;
            Q1=sQuery(id+"F2.wireOp",VERTEX,"E53.start");
            transform(context, id + "F13", {"entities" : qUnion([Q0]), "transformType" : TransformType.SCALE_UNIFORMLY, "scale" : .5, "scalePoint" : qUnion([Q1]), "makeCopy" : false});
        }
    });
